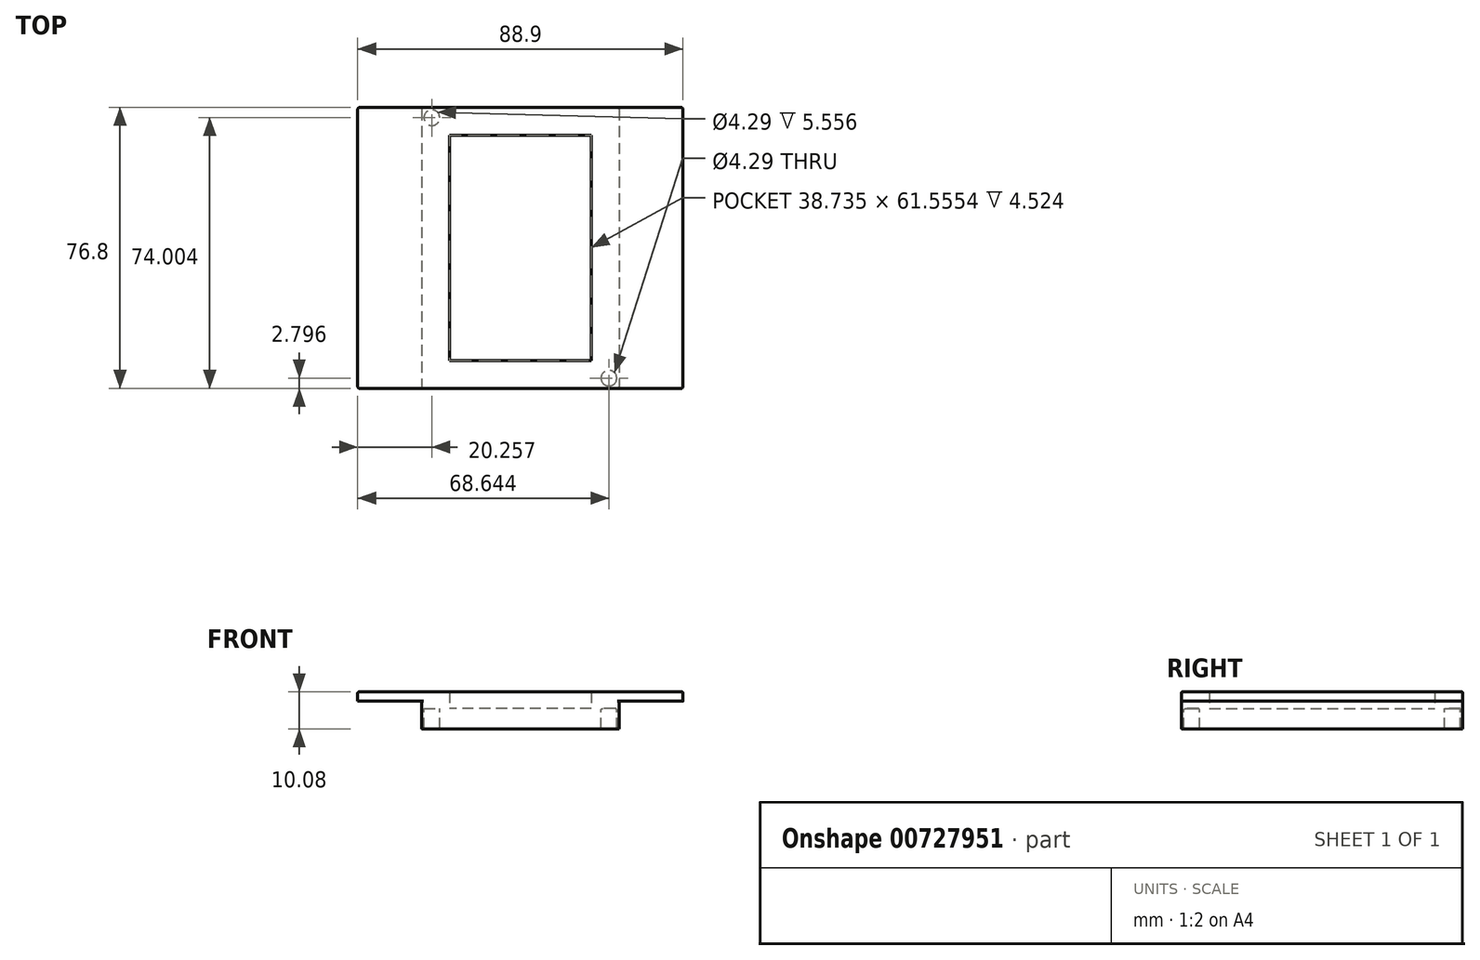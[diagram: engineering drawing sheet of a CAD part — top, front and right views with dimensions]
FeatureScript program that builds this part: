
annotation { "Feature Type Name" : "Feature", "Feature Type Description" : "" }
export const myFeature = defineFeature(function(context is Context, id is Id, definition is map)
    precondition{}
    {
        {
            var Q0;
            Q0=qCreatedBy(makeId("Top.planeOp"),FACE);
            var sketch = newSketch(context, id + "F0", { "sketchPlane" : qUnion([Q0])});
            skLineSegment(sketch, "E0", {"start": v(0, 0) * mm, "end": v(74.83, 0) * mm, "construction": true});
            skLineSegment(sketch, "E1", {"start": v(0, 0) * mm, "end": v(0, 69.35) * mm, "construction": true});
            skLineSegment(sketch, "E2.bottom", {"start": v(44.45, -38.4) * mm, "end": v(-44.45, -38.4) * mm});
            skLineSegment(sketch, "E2.top", {"start": v(44.45, 38.4) * mm, "end": v(-44.45, 38.4) * mm});
            skLineSegment(sketch, "E2.left", {"start": v(44.45, -38.4) * mm, "end": v(44.45, 38.4) * mm});
            skLineSegment(sketch, "E2.right", {"start": v(-44.45, -38.4) * mm, "end": v(-44.45, 38.4) * mm});
            skPoint(sketch, "E2.middle", {"position": v(0, 0) * mm});
            skLineSegment(sketch, "E3", {"start": v(-26.99, 38.4) * mm, "end": v(-26.99, -38.4) * mm});
            skLineSegment(sketch, "E4.MirrorCS", {"start": v(26.99, 38.4) * mm, "end": v(26.99, -38.4) * mm});
            skSolve(sketch);
        }
        {
            var Q0;
            Q0=makeQuery(id+"F0.imprint","IMPRINT",FACE,{"disambiguationData":[TD([[makeQuery(id+"F0.imprint","IMPRINT",EDGE,{"derivedFrom":sQuery(id+"F0.wireOp",EDGE,"E2.bottom")}),-1.0]])]});
            extrude(context, id + "F1", {"entities" : qUnion([Q0]), "depth" : 2.54 * mm, "offsetDistance" : 25.4 * mm});
        }
        {
            var Q0;
            {var subQ0=sQuery(id+"F0.wireOp",EDGE,"E3");Q0=makeQuery(id+"F0.imprint","IMPRINT",FACE,{"disambiguationData":[TD([[makeQuery(id+"F0.imprint","IMPRINT",EDGE,{"derivedFrom":subQ0}),1.0]])]});}
            extrude(context, id + "F2", {"entities" : qUnion([Q0]), "operationType" : NewBodyOperationType.ADD, "oppositeDirection" : true, "depth" : ((33 - 1.25) / 16) * mm, "offsetDistance" : 25.4 * mm});
        }
        {
            var Q0;
            Q0=makeQuery(id+"F2.opExtrude","CAP_FACE",FACE,{"disambiguationData":[OSD([sQuery(id+"F0.wireOp",EDGE,"E2.bottom"),sQuery(id+"F0.wireOp",EDGE,"E2.top"),sQuery(id+"F0.wireOp",EDGE,"E3"),sQuery(id+"F0.wireOp",EDGE,"E4.MirrorCS")])],"isStart":false});
            var sketch = newSketch(context, id + "F3", { "sketchPlane" : qUnion([Q0])});
            skCircle(sketch, "E5", {"center": v(-24.2, 35.6) * mm, "radius": 2.14 * mm});
            skLineSegment(sketch, "E6", {"start": v(0, 0) * mm, "end": v(0, 13.67) * mm, "construction": true});
            skLineSegment(sketch, "E7", {"start": v(0, 0) * mm, "end": v(12.15, 0) * mm, "construction": true});
            skCircle(sketch, "E8.MirrorC", {"center": v(24.2, 35.6) * mm, "radius": 2.14 * mm});
            skCircle(sketch, "E9.MirrorC", {"center": v(-24.2, -35.6) * mm, "radius": 2.14 * mm});
            skCircle(sketch, "E10.MirrorC", {"center": v(24.2, -35.6) * mm, "radius": 2.14 * mm});
            skSolve(sketch);
        }
        {
            var Q0;
            Q0=makeQuery(id+"F3.imprint","IMPRINT",FACE,{"disambiguationData":[TD([[makeQuery(id+"F3.imprint","IMPRINT",EDGE,{"derivedFrom":sQuery(id+"F3.wireOp",EDGE,"E5")}),1.0]])]});
            var Q1;
            Q1=makeQuery(id+"F3.imprint","IMPRINT",FACE,{"disambiguationData":[TD([[makeQuery(id+"F3.imprint","IMPRINT",EDGE,{"derivedFrom":sQuery(id+"F3.wireOp",EDGE,"E8.MirrorC")}),-1.0]])]});
            var Q2;
            Q2=makeQuery(id+"F3.imprint","IMPRINT",FACE,{"disambiguationData":[TD([[makeQuery(id+"F3.imprint","IMPRINT",EDGE,{"derivedFrom":sQuery(id+"F3.wireOp",EDGE,"E10.MirrorC")}),1.0]])]});
            var Q3;
            Q3=makeQuery(id+"F3.imprint","IMPRINT",FACE,{"disambiguationData":[TD([[makeQuery(id+"F3.imprint","IMPRINT",EDGE,{"derivedFrom":sQuery(id+"F3.wireOp",EDGE,"E9.MirrorC")}),-1.0]])]});
            extrude(context, id + "F4", {"entities" : qUnion([Q0, Q1, Q2, Q3]), "operationType" : NewBodyOperationType.ADD, "depth" : 5.56 * mm, "offsetDistance" : 25.4 * mm});
        }
        {
            var Q0;
            Q0=makeQuery(id+"F1.opExtrude","SWEPT_EDGE",EDGE,{"disambiguationData":[OSD([sQuery(id+"F0.wireOp",EDGE,"E2.bottom"),sQuery(id+"F0.wireOp",EDGE,"E2.left")])]});
            var Q1;
            Q1=makeQuery(id+"F1.opExtrude","SWEPT_EDGE",EDGE,{"disambiguationData":[OSD([sQuery(id+"F0.wireOp",EDGE,"E2.bottom"),sQuery(id+"F0.wireOp",EDGE,"E2.right")])]});
            var Q2;
            Q2=makeQuery(id+"F1.opExtrude","SWEPT_EDGE",EDGE,{"disambiguationData":[OSD([sQuery(id+"F0.wireOp",EDGE,"E2.top"),sQuery(id+"F0.wireOp",EDGE,"E2.left")])]});
            var Q3;
            Q3=makeQuery(id+"F1.opExtrude","SWEPT_EDGE",EDGE,{"disambiguationData":[OSD([sQuery(id+"F0.wireOp",EDGE,"E2.top"),sQuery(id+"F0.wireOp",EDGE,"E2.right")])]});
            fillet(context, id + "F5", {"entities" : qUnion([Q0, Q1, Q2, Q3]), "radius" : 0.5 * mm, "tangentPropagation" : true, "allowEdgeOverflow" : false});
        }
        {
            var Q0;
            Q0=makeQuery(id+"F1.opExtrude","CAP_EDGE",EDGE,{"disambiguationData":[OSD([sQuery(id+"F0.wireOp",EDGE,"E2.right")])],"isStart":false});
            fillet(context, id + "F6", {"entities" : qUnion([Q0]), "radius" : 0.25 * mm, "tangentPropagation" : true, "allowEdgeOverflow" : false});
        }
        {
            var Q0;
            Q0=makeQuery(id+"F2.opExtrude","SWEPT_EDGE",EDGE,{"disambiguationData":[OSD([sQuery(id+"F0.wireOp",EDGE,"E2.top"),sQuery(id+"F0.wireOp",EDGE,"E3")])]});
            var Q1;
            Q1=makeQuery(id+"F2.opExtrude","SWEPT_EDGE",EDGE,{"disambiguationData":[OSD([sQuery(id+"F0.wireOp",EDGE,"E2.bottom"),sQuery(id+"F0.wireOp",EDGE,"E3")])]});
            var Q2;
            Q2=makeQuery(id+"F2.opExtrude","SWEPT_EDGE",EDGE,{"disambiguationData":[OSD([sQuery(id+"F0.wireOp",EDGE,"E2.top"),sQuery(id+"F0.wireOp",EDGE,"E4.MirrorCS")])]});
            var Q3;
            Q3=makeQuery(id+"F2.opExtrude","SWEPT_EDGE",EDGE,{"disambiguationData":[OSD([sQuery(id+"F0.wireOp",EDGE,"E2.bottom"),sQuery(id+"F0.wireOp",EDGE,"E4.MirrorCS")])]});
            fillet(context, id + "F7", {"entities" : qUnion([Q0, Q1, Q2, Q3]), "radius" : 0.5 * mm, "tangentPropagation" : true, "allowEdgeOverflow" : false});
        }
        {
            var Q0;
            Q0=makeQuery(id+"F4.opExtrude","CAP_EDGE",EDGE,{"disambiguationData":[OSD([sQuery(id+"F3.wireOp",EDGE,"E8.MirrorC")])],"isStart":true});
            var Q1;
            Q1=makeQuery(id+"F4.opExtrude","CAP_EDGE",EDGE,{"disambiguationData":[OSD([sQuery(id+"F3.wireOp",EDGE,"E10.MirrorC")])],"isStart":true});
            var Q2;
            Q2=makeQuery(id+"F4.opExtrude","CAP_EDGE",EDGE,{"disambiguationData":[OSD([sQuery(id+"F3.wireOp",EDGE,"E5")])],"isStart":true});
            var Q3;
            Q3=makeQuery(id+"F4.opExtrude","CAP_EDGE",EDGE,{"disambiguationData":[OSD([sQuery(id+"F3.wireOp",EDGE,"E9.MirrorC")])],"isStart":true});
            fillet(context, id + "F8", {"entities" : qUnion([Q0, Q1, Q2, Q3]), "radius" : 0.5 * mm, "tangentPropagation" : true, "allowEdgeOverflow" : false});
        }
        {
            var Q0;
            Q0=makeQuery(id+"F2.opExtrude","CAP_FACE",FACE,{"disambiguationData":[OSD([sQuery(id+"F0.wireOp",EDGE,"E2.bottom"),sQuery(id+"F0.wireOp",EDGE,"E2.top"),sQuery(id+"F0.wireOp",EDGE,"E3"),sQuery(id+"F0.wireOp",EDGE,"E4.MirrorCS")])],"isStart":false});
            var sketch = newSketch(context, id + "F9", { "sketchPlane" : qUnion([Q0])});
            skLineSegment(sketch, "E11", {"start": v(0, 0) * mm, "end": v(57.95, 0) * mm, "construction": true});
            skPoint(sketch, "E11.endSnap0", {"position": v(26.99, 0) * mm});
            skLineSegment(sketch, "E12", {"start": v(0, 0) * mm, "end": v(0, -50.18) * mm, "construction": true});
            skPoint(sketch, "E12.endSnap0", {"position": v(0, -38.4) * mm});
            skLineSegment(sketch, "E13.bottom", {"start": v(19.37, 30.78) * mm, "end": v(-19.37, 30.78) * mm});
            skLineSegment(sketch, "E13.top", {"start": v(19.37, -30.78) * mm, "end": v(-19.37, -30.78) * mm});
            skLineSegment(sketch, "E13.left", {"start": v(19.37, 30.78) * mm, "end": v(19.37, -30.78) * mm});
            skLineSegment(sketch, "E13.right", {"start": v(-19.37, 30.78) * mm, "end": v(-19.37, -30.78) * mm});
            skPoint(sketch, "E13.middle", {"position": v(0, 0) * mm});
            skSolve(sketch);
        }
        {
            var Q0;
            Q0=makeQuery(id+"F9.imprint","IMPRINT",FACE,{"disambiguationData":[TD([[makeQuery(id+"F9.imprint","IMPRINT",EDGE,{"derivedFrom":sQuery(id+"F9.wireOp",EDGE,"E13.bottom")}),1.0]])]});
            extrude(context, id + "F10", {"entities" : qUnion([Q0]), "operationType" : NewBodyOperationType.REMOVE, "oppositeDirection" : true, "depth" : 45.72 * mm, "offsetDistance" : 25.4 * mm});
        }
    });
